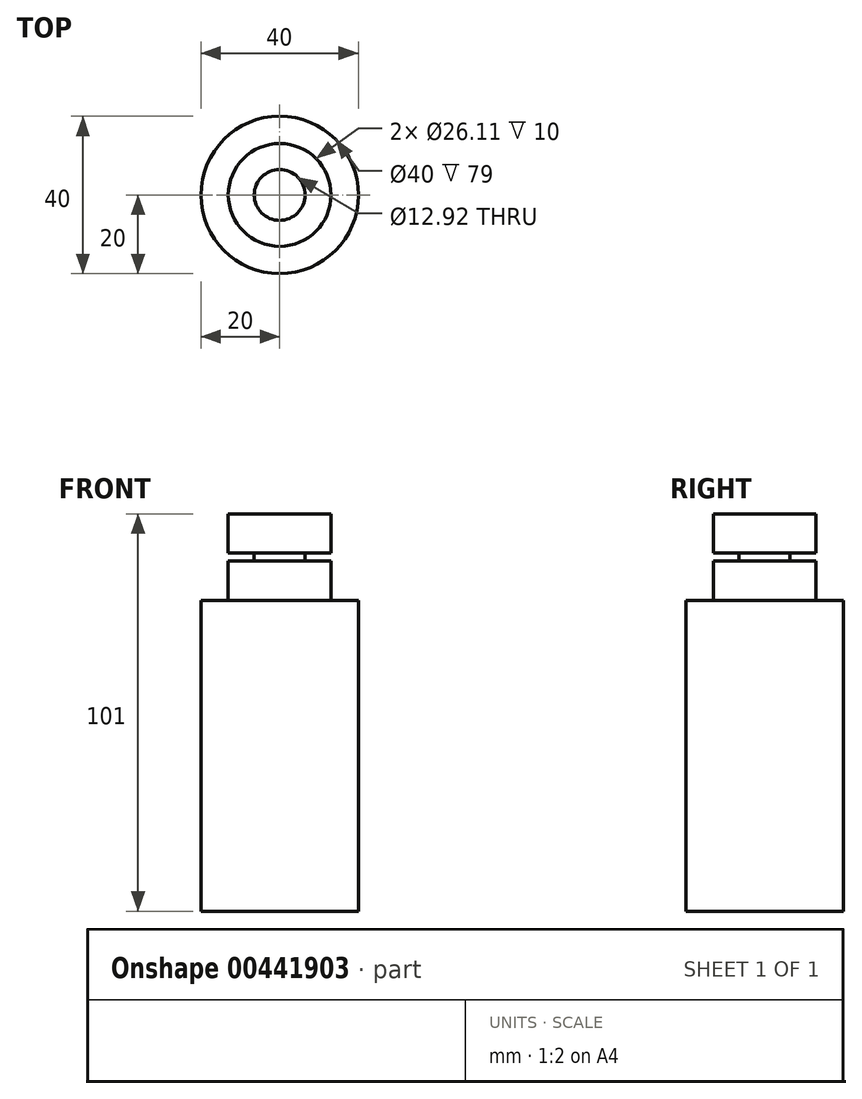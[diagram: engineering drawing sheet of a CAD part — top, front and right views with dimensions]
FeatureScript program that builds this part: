
annotation { "Feature Type Name" : "Feature", "Feature Type Description" : "" }
export const myFeature = defineFeature(function(context is Context, id is Id, definition is map)
    precondition{}
    {
        {
            var Q0;
            Q0=qCreatedBy(makeId("Front.planeOp"),FACE);
            var sketch = newSketch(context, id + "F0", { "sketchPlane" : qUnion([Q0])});
            skLineSegment(sketch, "E0", {"start": v(20, 0) * mm, "end": v(20, 79) * mm});
            skLineSegment(sketch, "E1", {"start": v(20, 79) * mm, "end": v(13.05, 79) * mm});
            skLineSegment(sketch, "E2", {"start": v(13.05, 79) * mm, "end": v(13.05, 89) * mm});
            skLineSegment(sketch, "E3", {"start": v(13.05, 89) * mm, "end": v(6.46, 89) * mm});
            skLineSegment(sketch, "E4", {"start": v(6.46, 89) * mm, "end": v(6.46, 91) * mm});
            skLineSegment(sketch, "E5", {"start": v(6.46, 91) * mm, "end": v(13.05, 91) * mm});
            skLineSegment(sketch, "E6", {"start": v(13.05, 91) * mm, "end": v(13.05, 101) * mm});
            skLineSegment(sketch, "E7", {"start": v(0, 0) * mm, "end": v(0, 124.92) * mm, "construction": true});
            skSolve(sketch);
        }
        {
            var Q0;
            Q0 = qSketchRegion(id + "F0", true);
            var Q1;
            Q1 = qConstructionFilter(qBodyType(qCreatedBy(id + "F0" ,EDGE), BodyType.WIRE), ConstructionObject.NO);
            var Q2;
            Q2=sQuery(id+"F0.wireOp",EDGE,"E7");
            revolve(context, id + "F1", {"bodyType" : ToolBodyType.SURFACE, "entities" : qUnion([Q0]), "surfaceEntities" : qUnion([Q1]), "axis" : qUnion([Q2]), "revolveType" : RevolveType.FULL});
        }
    });
